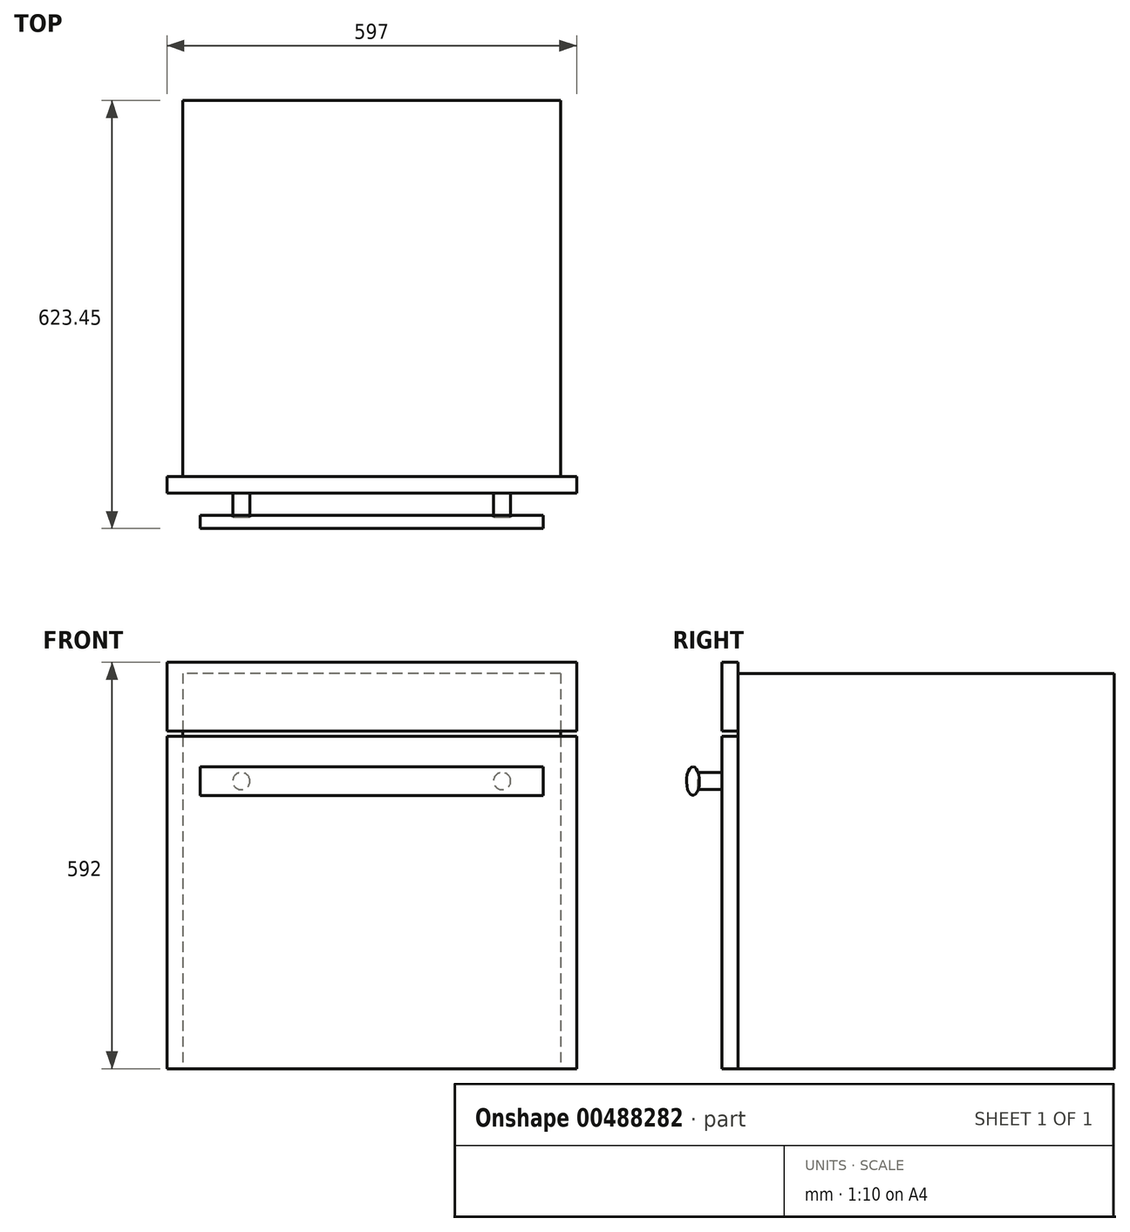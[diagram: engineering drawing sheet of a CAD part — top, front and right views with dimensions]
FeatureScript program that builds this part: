
annotation { "Feature Type Name" : "Feature", "Feature Type Description" : "" }
export const myFeature = defineFeature(function(context is Context, id is Id, definition is map)
    precondition{}
    {
        {
            var Q0;
            Q0=qCreatedBy(makeId("Top.planeOp"),FACE);
            var sketch = newSketch(context, id + "F0", { "sketchPlane" : qUnion([Q0])});
            skLineSegment(sketch, "E0.bottom", {"start": v(275, 274) * mm, "end": v(-275, 274) * mm});
            skLineSegment(sketch, "E0.top", {"start": v(275, -274) * mm, "end": v(-275, -274) * mm});
            skLineSegment(sketch, "E0.left", {"start": v(275, 274) * mm, "end": v(275, -274) * mm});
            skLineSegment(sketch, "E0.right", {"start": v(-275, 274) * mm, "end": v(-275, -274) * mm});
            skPoint(sketch, "E0.middle", {"position": v(0, 0) * mm});
            skSolve(sketch);
        }
        {
            var Q0;
            Q0 = qSketchRegion(id + "F0", true);
            extrude(context, id + "F1", {"entities" : qUnion([Q0]), "depth" : 576 * mm});
        }
        {
            var Q0;
            Q0=makeQuery(id+"F1.opExtrude","SWEPT_FACE",FACE,{"disambiguationData":[OSD([sQuery(id+"F0.wireOp",EDGE,"E0.top")])]});
            var sketch = newSketch(context, id + "F2", { "sketchPlane" : qUnion([Q0])});
            skLineSegment(sketch, "E1.bottom", {"start": v(298.5, 492) * mm, "end": v(-298.5, 492) * mm});
            skLineSegment(sketch, "E1.top", {"start": v(298.5, 592) * mm, "end": v(-298.5, 592) * mm});
            skLineSegment(sketch, "E1.left", {"start": v(298.5, 492) * mm, "end": v(298.5, 592) * mm});
            skLineSegment(sketch, "E1.right", {"start": v(-298.5, 492) * mm, "end": v(-298.5, 592) * mm});
            skPoint(sketch, "E1.middle", {"position": v(0, 542) * mm});
            skLineSegment(sketch, "E2.bottom", {"start": v(298.5, 0) * mm, "end": v(-298.5, 0) * mm});
            skLineSegment(sketch, "E2.top", {"start": v(298.5, 484) * mm, "end": v(-298.5, 484) * mm});
            skLineSegment(sketch, "E2.left", {"start": v(298.5, 0) * mm, "end": v(298.5, 484) * mm});
            skLineSegment(sketch, "E2.right", {"start": v(-298.5, 0) * mm, "end": v(-298.5, 484) * mm});
            skPoint(sketch, "E2.middle", {"position": v(0, 242) * mm});
            skSolve(sketch);
        }
        {
            var Q0;
            Q0 = qSketchRegion(id + "F2", true);
            extrude(context, id + "F3", {"entities" : qUnion([Q0]), "depth" : 24 * mm});
        }
        {
            var Q0;
            Q0=makeQuery(id+"F3.opExtrude","CAP_FACE",FACE,{"disambiguationData":[OSD([sQuery(id+"F2.wireOp",EDGE,"E2.bottom"),sQuery(id+"F2.wireOp",EDGE,"E2.top"),sQuery(id+"F2.wireOp",EDGE,"E2.left"),sQuery(id+"F2.wireOp",EDGE,"E2.right")])],"isStart":false});
            var sketch = newSketch(context, id + "F4", { "sketchPlane" : qUnion([Q0])});
            skLineSegment(sketch, "E3", {"start": v(0, 0) * mm, "end": v(0, 484) * mm, "construction": true});
            skLineSegment(sketch, "E4", {"start": v(-298.5, 419) * mm, "end": v(298.5, 419) * mm, "construction": true});
            skCircle(sketch, "E5", {"center": v(-190, 419) * mm, "radius": 12.5 * mm});
            skCircle(sketch, "E6", {"center": v(190, 419) * mm, "radius": 12.5 * mm});
            skSolve(sketch);
        }
        {
            var Q0;
            Q0 = qSketchRegion(id + "F4", true);
            extrude(context, id + "F5", {"entities" : qUnion([Q0]), "operationType" : NewBodyOperationType.ADD, "depth" : 35 * mm});
        }
        {
            var Q0;
            Q0=qCreatedBy(makeId("Right.planeOp"),FACE);
            var sketch = newSketch(context, id + "F6", { "sketchPlane" : qUnion([Q0])});
            skEllipse(sketch, "E7", {"center": v(-340, 419) * mm, "majorRadius": 20.93 * mm, "minorRadius": 9.45 * mm, "majorAxis": v(0, 1)});
            skSolve(sketch);
        }
        {
            var Q0;
            Q0 = qSketchRegion(id + "F6", true);
            extrude(context, id + "F7", {"entities" : qUnion([Q0]), "depth" : 250 * mm, "hasSecondDirection" : true, "secondDirectionOppositeDirection" : true, "secondDirectionDepth" : 250 * mm});
        }
    });
